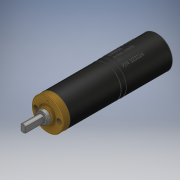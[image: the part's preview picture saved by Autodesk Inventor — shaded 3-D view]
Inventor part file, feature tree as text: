
AUTODESK INVENTOR PART (.ipt)
format: ipt  version: 2019.2 (Build 232265000, 265)  size: 1,871,360 bytes
history: native  units: mm
features: extrude x12, sketch x6, chamfer x2, thread x2, fillet x1, plane x1, emboss x1, projected_geometry x1
ambient origin geometry x8: Origin, YZ Plane, XZ Plane, XY Plane, X Axis, Y Axis, Z Axis, Center Point
bodies: Solid1 (feature_tree), Solid2 (feature_tree), Solid3 (feature_tree), Solid4 (feature_tree), Solid5 (feature_tree)
feature tree (26):
  sketch  "Sketch1"  dims[d0=12.9mm d1=11.0mm]
  extrude  "Extrusion1"  Depth=11.0mm
  extrude  "Extrusion2"  Depth=2.35mm TaperAngle=0.0deg
  sketch  "Sketch2"  dims[d2=20.9mm d3=0.0mm d4=2.35mm d5=0.0mm]
  extrude  "Extrusion3"  Depth=2.8mm TaperAngle=0.0deg
  sketch  "Sketch3"  dims[d6=12.85mm d7=2.8mm d8=0.0mm]
  extrude  "Extrusion4"  Depth=2.0mm
  extrude  "Extrusion5"  Depth=6.0mm
  extrude  "Extrusion6"  Depth=10.0mm
  extrude  "Extrusion7"  Depth=2.5mm TaperAngle=0.0deg
  extrude  "Extrusion8"  Depth=10.0mm TaperAngle=0.0deg
  extrude  "Extrusion9"  Depth=10.0mm TaperAngle=0.0deg
  extrude  "Extrusion10"  Depth=10.0mm TaperAngle=0.0deg
  chamfer  "Chamfer1"  Distance=5.0mm
  fillet  "Fillet1"  Radius=3.0mm
  thread  "Thread1"  [1 undecoded]
  thread  "Thread2"  [1 undecoded]
  extrude  "Extrusion11"  Depth=10.0mm
  sketch  "Sketch5"  dims[d11=1.0mm d12=6.0mm]
  extrude  "Extrusion12"  Depth=10.0mm TaperAngle=0.0deg
  chamfer  "Chamfer2"  Distance=0.2mm Angle=45.0deg
  plane  "Work Plane1"
  emboss  "Emboss1"
  sketch  "Sketch4"  dims[d9=2.0mm d10=2.0mm]
  sketch  "Sketch6"  dims[d13=4.75mm d14=7.0mm d15=2.5mm d16=0.0mm d17=0.2mm d18=0.0mm d19=0.2mm d20=0.0mm d21=1.0mm d22=0.0mm d23=5.0mm d24=3.0mm d25=2.6mm d26=0.0mm d27=10.0mm d28=0.0mm d29=2.0mm d30=7.0mm d31=0.0mm d32=0.2mm d33=2.0mm d34=45.0deg d35=0.2mm d36=10.0mm d37=0.0mm d38=10.0mm d39=0.0mm d40=0.2mm d41=2.0mm d42=45.0deg d43=21.0mm d44=0.0mm d45=13.0mm d46=19.0mm d47=0.0mm d48=0.05mm d49=0.0mm]
  projected_geometry  "Projected Loop1"
note: 2 required parameter values undecoded (feature->parameter linkage not recoverable at this tier; creation-order binding heuristic only, values carry confidence <= 0.55)
